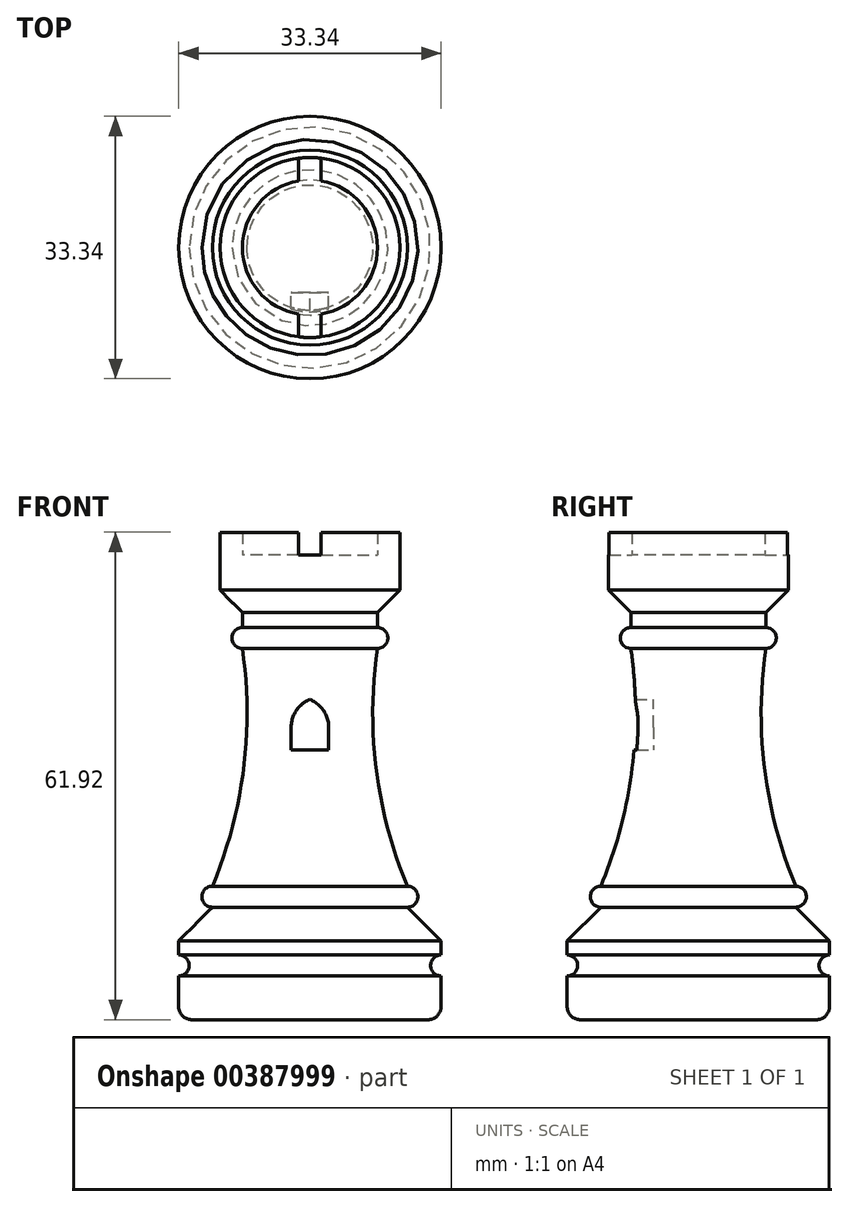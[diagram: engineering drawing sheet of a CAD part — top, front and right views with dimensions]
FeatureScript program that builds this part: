
annotation { "Feature Type Name" : "Feature", "Feature Type Description" : "" }
export const myFeature = defineFeature(function(context is Context, id is Id, definition is map)
    precondition{}
    {
        {
            var Q0;
            Q0=qCreatedBy(makeId("Front.planeOp"),FACE);
            var sketch = newSketch(context, id + "F0", { "sketchPlane" : qUnion([Q0])});
            skLineSegment(sketch, "E0", {"start": v(0, 0) * mm, "end": v(16.51, 0) * mm});
            skLineSegment(sketch, "E1", {"start": v(16.51, 0) * mm, "end": v(22.23, -5.71) * mm});
            skLineSegment(sketch, "E2", {"start": v(22.22, -5.71) * mm, "end": v(22.22, -8.1) * mm});
            skArc(sketch, "E3", {"start": v(22.23, -8.1) * mm, "mid": v(20.45, -9.88) * mm, "end": v(22.23, -11.66) * mm});
            skLineSegment(sketch, "E4", {"start": v(22.23, -11.66) * mm, "end": v(22.23, -19.05) * mm});
            skLineSegment(sketch, "E5", {"start": v(22.23, -19.05) * mm, "end": v(0, -19.05) * mm});
            skLineSegment(sketch, "E6", {"start": v(0, -19.05) * mm, "end": v(0, 0) * mm});
            skSolve(sketch);
        }
        {
            var Q0;
            Q0=makeQuery(id+"F0.imprint","IMPRINT",FACE,{"disambiguationData":[TD([[makeQuery(id+"F0.imprint","IMPRINT",EDGE,{"derivedFrom":sQuery(id+"F0.wireOp",EDGE,"E0")}),-1.0]])]});
            var Q1;
            Q1=sQuery(id+"F0.wireOp",EDGE,"E6");
            revolve(context, id + "F1", {"entities" : qUnion([Q0]), "axis" : qUnion([Q1]), "revolveType" : RevolveType.FULL});
        }
        {
            var Q0;
            Q0=qCreatedBy(makeId("Front.planeOp"),FACE);
            var sketch = newSketch(context, id + "F2", { "sketchPlane" : qUnion([Q0])});
            skLineSegment(sketch, "E7", {"start": v(0, 0) * mm, "end": v(0, 59.7) * mm});
            skLineSegment(sketch, "E8", {"start": v(0, 59.7) * mm, "end": v(11.43, 59.7) * mm});
            skLineSegment(sketch, "E9", {"start": v(11.43, 59.7) * mm, "end": v(11.43, 63.5) * mm});
            skLineSegment(sketch, "E10", {"start": v(11.43, 63.5) * mm, "end": v(15.24, 63.5) * mm});
            skLineSegment(sketch, "E11", {"start": v(15.24, 63.5) * mm, "end": v(15.24, 53.72) * mm});
            skLineSegment(sketch, "E12", {"start": v(15.24, 53.72) * mm, "end": v(11.43, 49.91) * mm});
            skLineSegment(sketch, "E13", {"start": v(11.43, 49.91) * mm, "end": v(11.43, 47.37) * mm});
            skArc(sketch, "E14", {"start": v(11.43, 43.81) * mm, "mid": v(13.2, 45.6) * mm, "end": v(11.43, 47.37) * mm});
            skArc(sketch, "E15", {"start": v(11.43, 43.81) * mm, "mid": v(11.24, 23.34) * mm, "end": v(16.5, 3.56) * mm});
            skArc(sketch, "E16", {"start": v(16.51, 0) * mm, "mid": v(18.29, 1.78) * mm, "end": v(16.51, 3.56) * mm});
            skLineSegment(sketch, "E17", {"start": v(16.51, 0) * mm, "end": v(0, 0) * mm});
            skSolve(sketch);
        }
        {
            var Q0;
            Q0 = qSketchRegion(id + "F2", true);
            var Q1;
            Q1=sQuery(id+"F2.wireOp",EDGE,"E7");
            revolve(context, id + "F3", {"operationType" : NewBodyOperationType.ADD, "entities" : qUnion([Q0]), "axis" : qUnion([Q1]), "revolveType" : RevolveType.FULL});
        }
        {
            var Q0;
            Q0=qCreatedBy(makeId("Front.planeOp"),FACE);
            var sketch = newSketch(context, id + "F4", { "sketchPlane" : qUnion([Q0])});
            skLineSegment(sketch, "E18.bottom", {"start": v(1.9, 59.7) * mm, "end": v(-1.9, 59.7) * mm});
            skLineSegment(sketch, "E18.top", {"start": v(1.9, 63.5) * mm, "end": v(-1.9, 63.5) * mm});
            skLineSegment(sketch, "E18.left", {"start": v(1.9, 59.7) * mm, "end": v(1.9, 63.5) * mm});
            skLineSegment(sketch, "E18.right", {"start": v(-1.9, 59.7) * mm, "end": v(-1.9, 63.5) * mm});
            skPoint(sketch, "E18.middle", {"position": v(0, 61.6) * mm});
            skSolve(sketch);
        }
        {
            var Q0;
            Q0 = qSketchRegion(id + "F4", true);
            extrude(context, id + "F5", {"entities" : qUnion([Q0]), "operationType" : NewBodyOperationType.REMOVE, "endBound" : BoundingType.THROUGH_ALL, "depth" : 25.4 * mm, "offsetDistance" : 25.4 * mm, "hasSecondDirection" : true, "secondDirectionBound" : BoundingType.THROUGH_ALL, "secondDirectionOppositeDirection" : true, "secondDirectionDepth" : 25.4 * mm});
        }
        {
            var Q0;
            Q0=qCreatedBy(makeId("Front.planeOp"),FACE);
            cPlane(context, id + "F6", {"entities" : qUnion([Q0]), "cplaneType" : CPlaneType.OFFSET, "offset" : 7.62 * mm, "width" : 152.4 * mm, "height" : 152.4 * mm});
        }
        {
            var Q0;
            Q0=qCreatedBy(id+"F6.planeOp",FACE);
            var sketch = newSketch(context, id + "F7", { "sketchPlane" : qUnion([Q0])});
            skLineSegment(sketch, "E19", {"start": v(-3.18, 30.48) * mm, "end": v(-1.9, 30.48) * mm, "construction": true});
            skLineSegment(sketch, "E20", {"start": v(-1.9, 30.48) * mm, "end": v(-0.64, 30.48) * mm, "construction": true});
            skLineSegment(sketch, "E21", {"start": v(-0.64, 30.48) * mm, "end": v(0.64, 30.48) * mm, "construction": true});
            skLineSegment(sketch, "E22", {"start": v(0.64, 30.48) * mm, "end": v(1.9, 30.48) * mm, "construction": true});
            skLineSegment(sketch, "E23", {"start": v(1.9, 30.48) * mm, "end": v(3.18, 30.48) * mm, "construction": true});
            skPoint(sketch, "E24", {"position": v(0, 30.48) * mm});
            skArc(sketch, "E25", {"start": v(-3.18, 30.48) * mm, "mid": v(-2.3, 33.32) * mm, "end": v(0, 35.19) * mm});
            skArc(sketch, "E26", {"start": v(3.18, 30.48) * mm, "mid": v(2.3, 33.32) * mm, "end": v(0, 35.19) * mm});
            skLineSegment(sketch, "E27", {"start": v(-3.18, 30.48) * mm, "end": v(-3.18, 26.67) * mm});
            skLineSegment(sketch, "E28", {"start": v(-3.18, 26.67) * mm, "end": v(3.18, 26.67) * mm});
            skLineSegment(sketch, "E29", {"start": v(3.18, 26.67) * mm, "end": v(3.18, 30.48) * mm});
            skSolve(sketch);
        }
        {
            var Q0;
            Q0 = qSketchRegion(id + "F7", true);
            extrude(context, id + "F8", {"entities" : qUnion([Q0]), "operationType" : NewBodyOperationType.REMOVE, "endBound" : BoundingType.THROUGH_ALL, "depth" : 25.4 * mm, "offsetDistance" : 25.4 * mm});
        }
        {
            var Q0;
            Q0=makeQuery(id+"F1.opRevolve","SWEPT_EDGE",EDGE,{"disambiguationData":[OSD([sQuery(id+"F0.wireOp",EDGE,"E4"),sQuery(id+"F0.wireOp",EDGE,"E5")])]});
            fillet(context, id + "F9", {"entities" : qUnion([Q0]), "tangentPropagation" : true, "radius" : 2.22 * mm, "defaultsChanged" : true, "vertexSettings" : [], "allowEdgeOverflow" : false});
        }
        {
            var Q0;
            Q0=makeQuery(id+"F1.opRevolve","SWEPT_BODY",BODY,{"disambiguationData":[OSD([sQuery(id+"F0.wireOp",EDGE,"E0"),sQuery(id+"F0.wireOp",EDGE,"E1"),sQuery(id+"F0.wireOp",EDGE,"E2"),sQuery(id+"F0.wireOp",EDGE,"E3"),sQuery(id+"F0.wireOp",EDGE,"E4"),sQuery(id+"F0.wireOp",EDGE,"E5"),sQuery(id+"F0.wireOp",EDGE,"E6")])]});
            var Q1;
            Q1=sQuery(id+"F0.wireOp",VERTEX,"E6.end");
            transform(context, id + "F10", {"entities" : qUnion([Q0]), "transformType" : TransformType.SCALE_UNIFORMLY, "scale" : .75, "scalePoint" : qUnion([Q1]), "makeCopy" : false});
        }
    });
